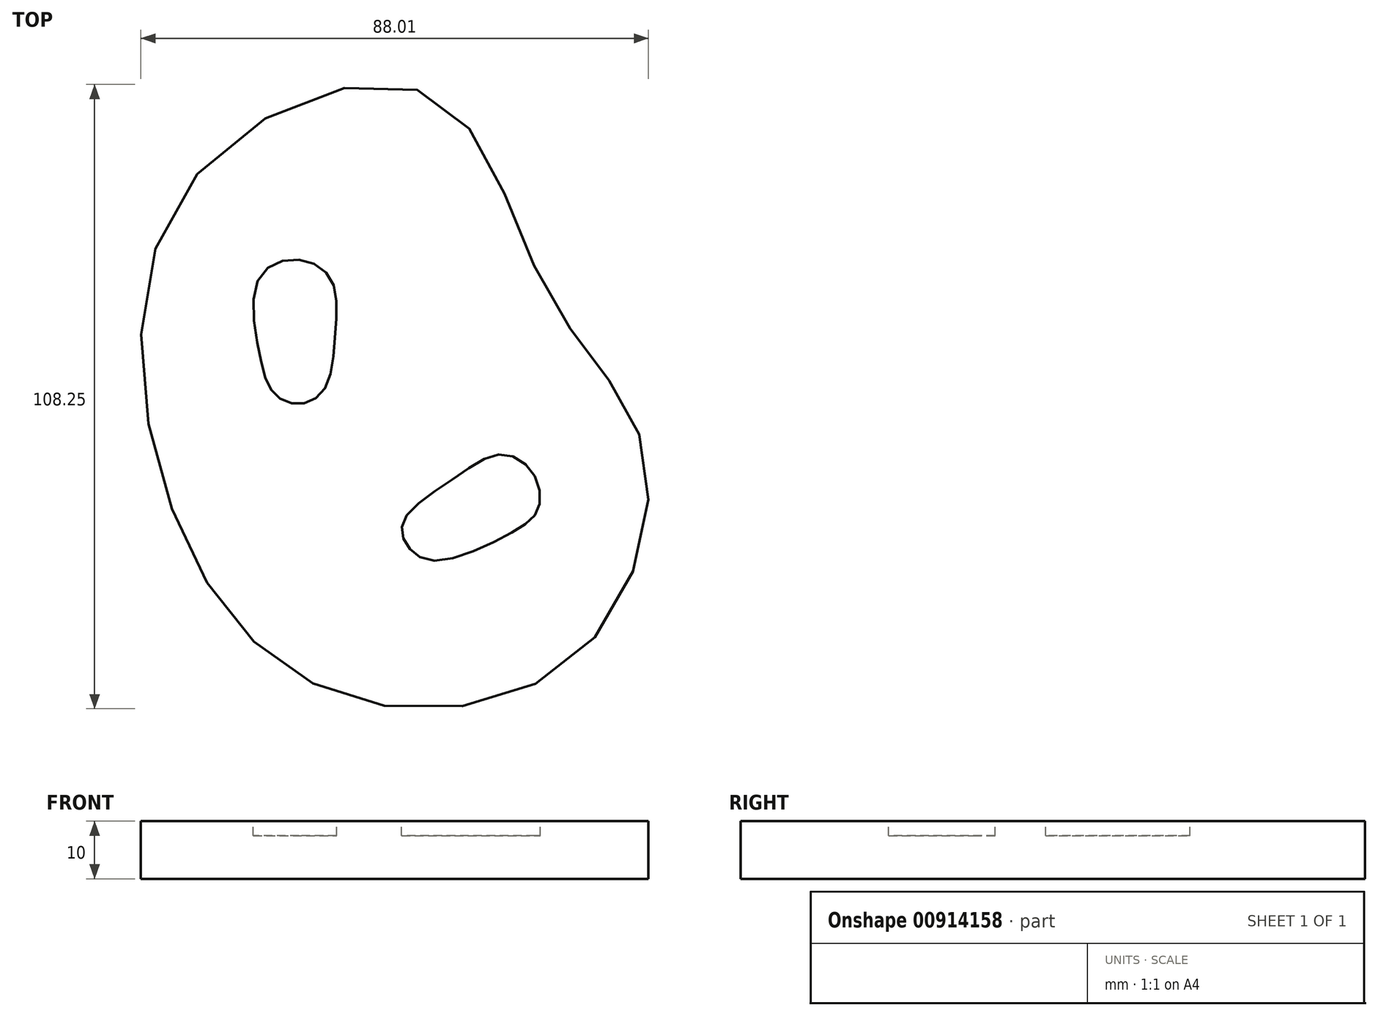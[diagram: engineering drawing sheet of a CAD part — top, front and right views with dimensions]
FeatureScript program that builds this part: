
annotation { "Feature Type Name" : "Feature", "Feature Type Description" : "" }
export const myFeature = defineFeature(function(context is Context, id is Id, definition is map)
    precondition{}
    {
        {
            assignVariable(context, id + "F0", {"name" : "h", "anyValue" : 10});
        }
        {
            var Q0;
            Q0=qCreatedBy(makeId("Top.planeOp"),FACE);
            var sketch = newSketch(context, id + "F1", { "sketchPlane" : qUnion([Q0])});
            skFitSpline(sketch, "E0", {"points": [v(-10.35, 25.21) * mm, v(-17.36, 21.86) * mm, v(-17.11, 8.64) * mm, v(-14.67, 2) * mm, v(-10.22, 0.21) * mm, v(-5.84, 2.85) * mm, v(-4.07, 12.17) * mm, v(-4.62, 21.5) * mm, v(-10.35, 25.21) * mm]});
            skFitSpline(sketch, "E1", {"points": [v(30.6, -12.37) * mm, v(25.06, -8.55) * mm, v(16.65, -12.63) * mm, v(7.87, -19.95) * mm, v(8.26, -24.1) * mm, v(13.05, -27.02) * mm, v(26.1, -22.38) * mm, v(31.03, -18.3) * mm, v(30.6, -12.37) * mm]});
            skFitSpline(sketch, "E2", {"points": [v(-32.35, -18.03) * mm, v(-30.03, 37.4) * mm, v(12.27, 53.8) * mm, v(32.75, 19.5) * mm, v(49.52, -8) * mm, v(37.14, -44.12) * mm, v(-4.42, -49.84) * mm, v(-32.35, -18.03) * mm]});
            skLineSegment(sketch, "E3", {"start": v(-10.35, 25.21) * mm, "end": v(-10.22, 0.21) * mm, "construction": true});
            skLineSegment(sketch, "E4", {"start": v(8.26, -24.1) * mm, "end": v(30.6, -12.37) * mm, "construction": true});
            skFitSpline(sketch, "E5.0", {"points": [v(-25.37, -18.06) * mm, v(-26.26, -15.78) * mm, v(-27.1, -13.42) * mm, v(-28.13, -10.2) * mm, v(-29.26, -6.07) * mm, v(-30.3, -1) * mm, v(-31.23, 5.83) * mm, v(-31.38, 12.6) * mm, v(-30.64, 19) * mm, v(-29.61, 23.58) * mm, v(-28.1, 27.85) * mm, v(-26.58, 30.8) * mm, v(-25.4, 32.68) * mm, v(-24.79, 33.59) * mm, v(-24.13, 34.48) * mm, v(-23.2, 35.65) * mm, v(-21.92, 37.08) * mm, v(-19.7, 39.27) * mm, v(-16.63, 41.8) * mm, v(-12.58, 44.39) * mm, v(-8.33, 46.48) * mm, v(-4.06, 48) * mm, v(0.06, 48.9) * mm, v(3.2, 49.14) * mm, v(5.43, 49.02) * mm, v(6.95, 48.79) * mm, v(8.07, 48.5) * mm, v(8.88, 48.2) * mm, v(9.44, 47.96) * mm, v(9.97, 47.7) * mm, v(10.66, 47.29) * mm, v(11.5, 46.67) * mm, v(12.52, 45.76) * mm, v(13.86, 44.28) * mm, v(15.51, 41.93) * mm, v(17.41, 38.43) * mm, v(19.24, 34.4) * mm, v(21.03, 30) * mm, v(22.56, 26.15) * mm, v(23.85, 23.05) * mm, v(24.88, 20.72) * mm, v(25.8, 18.8) * mm, v(26.56, 17.27) * mm, v(27.17, 16.13) * mm, v(27.8, 15.03) * mm, v(28.64, 13.6) * mm, v(29.73, 11.88) * mm, v(31.05, 9.94) * mm, v(32.8, 7.5) * mm, v(34.96, 4.66) * mm, v(37.35, 1.55) * mm, v(39.44, -1.36) * mm, v(40.86, -3.67) * mm, v(41.79, -5.48) * mm, v(42.38, -6.84) * mm, v(42.78, -7.98) * mm, v(43.05, -8.91) * mm, v(43.23, -9.62) * mm, v(43.38, -10.36) * mm, v(43.55, -11.39) * mm, v(43.7, -12.74) * mm, v(43.78, -14.45) * mm, v(43.73, -16.83) * mm, v(43.38, -19.95) * mm, v(42.5, -23.79) * mm, v(41.19, -27.58) * mm, v(39.45, -31.2) * mm, v(37.67, -34) * mm, v(36.08, -36.03) * mm, v(34.8, -37.45) * mm, v(33.67, -38.54) * mm, v(32.74, -39.34) * mm, v(31.28, -40.5) * mm, v(28.9, -42.05) * mm, v(25.36, -43.73) * mm, v(21.52, -44.98) * mm, v(16.1, -46.09) * mm, v(10.43, -46.32) * mm, v(4.9, -45.7) * mm, v(1.56, -44.97) * mm, v(-0.97, -44.19) * mm, v(-2.8, -43.52) * mm, v(-4.54, -42.75) * mm, v(-6.8, -41.6) * mm, v(-9.46, -39.95) * mm, v(-13.43, -36.8) * mm, v(-17.91, -31.95) * mm, v(-21.77, -25.86) * mm, v(-24.13, -21) * mm, v(-25.37, -18.06) * mm, v(-26.26, -15.78) * mm, v(-27.1, -13.42) * mm, v(-25.37, -18.06) * mm]});
            skFitSpline(sketch, "E6.0", {"points": [v(-21.2, -16.37) * mm, v(-22.04, -14.21) * mm, v(-22.83, -11.98) * mm, v(-23.8, -8.94) * mm, v(-24.88, -5.02) * mm, v(-25.86, -0.23) * mm, v(-26.52, 4.57) * mm, v(-26.8, 9.31) * mm, v(-26.7, 13.9) * mm, v(-26.2, 18.27) * mm, v(-25.27, 22.34) * mm, v(-24.17, 25.46) * mm, v(-23.08, 27.77) * mm, v(-22.31, 29.15) * mm, v(-21.65, 30.2) * mm, v(-21.12, 30.98) * mm, v(-20.56, 31.74) * mm, v(-19.75, 32.74) * mm, v(-18.66, 33.98) * mm, v(-16.72, 35.9) * mm, v(-13.98, 38.14) * mm, v(-10.36, 40.46) * mm, v(-6.57, 42.33) * mm, v(-2.8, 43.67) * mm, v(0.15, 44.32) * mm, v(2.28, 44.55) * mm, v(3.73, 44.6) * mm, v(5, 44.53) * mm, v(5.89, 44.4) * mm, v(6.49, 44.26) * mm, v(6.89, 44.14) * mm, v(7.24, 44.01) * mm, v(7.53, 43.89) * mm, v(7.8, 43.75) * mm, v(8.07, 43.59) * mm, v(8.36, 43.4) * mm, v(8.76, 43.09) * mm, v(9.31, 42.59) * mm, v(10.04, 41.78) * mm, v(10.83, 40.75) * mm, v(11.94, 39.08) * mm, v(13.36, 36.46) * mm, v(15.1, 32.64) * mm, v(16.55, 29.05) * mm, v(17.77, 26.01) * mm, v(18.72, 23.67) * mm, v(19.72, 21.28) * mm, v(20.6, 19.26) * mm, v(21.36, 17.64) * mm, v(21.95, 16.42) * mm, v(22.57, 15.2) * mm, v(23.23, 13.97) * mm, v(23.9, 12.78) * mm, v(24.8, 11.24) * mm, v(25.97, 9.41) * mm, v(27.36, 7.36) * mm, v(28.74, 5.44) * mm, v(30.08, 3.65) * mm, v(31.8, 1.4) * mm, v(33.76, -1.16) * mm, v(35.71, -3.89) * mm, v(36.95, -5.91) * mm, v(37.72, -7.41) * mm, v(38.19, -8.5) * mm, v(38.5, -9.37) * mm, v(38.7, -10.08) * mm, v(38.84, -10.62) * mm, v(38.96, -11.19) * mm, v(39.1, -12) * mm, v(39.21, -13.08) * mm, v(39.27, -14.5) * mm, v(39.23, -16.5) * mm, v(38.94, -19.2) * mm, v(38.17, -22.54) * mm, v(37.02, -25.86) * mm, v(35.5, -29.02) * mm, v(33.97, -31.42) * mm, v(32.62, -33.14) * mm, v(31.56, -34.33) * mm, v(30.63, -35.22) * mm, v(29.87, -35.87) * mm, v(29.08, -36.5) * mm, v(28.02, -37.25) * mm, v(26.2, -38.34) * mm, v(23.7, -39.53) * mm, v(20.37, -40.62) * mm, v(16.8, -41.35) * mm, v(13.08, -41.7) * mm, v(9.32, -41.66) * mm, v(6.24, -41.32) * mm, v(3.86, -40.86) * mm, v(2.13, -40.43) * mm, v(0.47, -39.92) * mm, v(-1.11, -39.34) * mm, v(-2.62, -38.68) * mm, v(-4.56, -37.7) * mm, v(-6.86, -36.26) * mm, v(-10.32, -33.53) * mm, v(-13.5, -30.09) * mm, v(-16.42, -25.89) * mm, v(-18.46, -22.37) * mm, v(-20.03, -19.13) * mm, v(-21.2, -16.37) * mm, v(-22.04, -14.21) * mm, v(-22.83, -11.98) * mm, v(-21.2, -16.37) * mm]});
            skFitSpline(sketch, "E7.0", {"points": [v(-18.42, -15.24) * mm, v(-19.23, -13.17) * mm, v(-19.99, -11.02) * mm, v(-20.93, -8.1) * mm, v(-21.96, -4.33) * mm, v(-22.9, 0.28) * mm, v(-23.53, 4.87) * mm, v(-23.8, 9.37) * mm, v(-23.7, 13.7) * mm, v(-23.23, 17.77) * mm, v(-22.38, 21.52) * mm, v(-21.38, 24.33) * mm, v(-20.4, 26.4) * mm, v(-19.73, 27.62) * mm, v(-19.14, 28.56) * mm, v(-18.67, 29.24) * mm, v(-18.18, 29.9) * mm, v(-17.46, 30.8) * mm, v(-16.48, 31.91) * mm, v(-14.72, 33.65) * mm, v(-12.22, 35.7) * mm, v(-8.88, 37.84) * mm, v(-5.39, 39.56) * mm, v(-1.95, 40.78) * mm, v(0.68, 41.36) * mm, v(2.5, 41.56) * mm, v(3.7, 41.6) * mm, v(4.7, 41.54) * mm, v(5.34, 41.44) * mm, v(5.73, 41.35) * mm, v(5.97, 41.28) * mm, v(6.11, 41.23) * mm, v(6.2, 41.2) * mm, v(6.28, 41.16) * mm, v(6.34, 41.12) * mm, v(6.46, 41.05) * mm, v(6.6, 40.96) * mm, v(6.82, 40.8) * mm, v(7.18, 40.47) * mm, v(7.72, 39.87) * mm, v(8.38, 39.02) * mm, v(9.34, 37.56) * mm, v(10.67, 35.14) * mm, v(12.33, 31.47) * mm, v(13.77, 27.93) * mm, v(14.99, 24.9) * mm, v(15.94, 22.53) * mm, v(16.96, 20.1) * mm, v(17.87, 18.03) * mm, v(18.65, 16.35) * mm, v(19.26, 15.09) * mm, v(19.91, 13.81) * mm, v(20.6, 12.53) * mm, v(21.3, 11.27) * mm, v(22.02, 10.07) * mm, v(22.74, 8.9) * mm, v(23.7, 7.4) * mm, v(24.9, 5.64) * mm, v(26.32, 3.67) * mm, v(27.69, 1.84) * mm, v(29.42, -0.43) * mm, v(31.36, -2.96) * mm, v(32.91, -5.14) * mm, v(33.9, -6.67) * mm, v(34.51, -7.73) * mm, v(35, -8.7) * mm, v(35.33, -9.45) * mm, v(35.55, -10.02) * mm, v(35.69, -10.44) * mm, v(35.8, -10.87) * mm, v(35.91, -11.28) * mm, v(36, -11.74) * mm, v(36.12, -12.4) * mm, v(36.22, -13.3) * mm, v(36.27, -14.52) * mm, v(36.24, -16.28) * mm, v(35.97, -18.68) * mm, v(35.28, -21.7) * mm, v(34.24, -24.72) * mm, v(32.87, -27.57) * mm, v(31.5, -29.7) * mm, v(30.32, -31.21) * mm, v(29.4, -32.24) * mm, v(28.6, -33) * mm, v(27.96, -33.56) * mm, v(27.29, -34.1) * mm, v(26.38, -34.73) * mm, v(24.8, -35.68) * mm, v(22.6, -36.73) * mm, v(19.6, -37.71) * mm, v(16.36, -38.38) * mm, v(12.96, -38.7) * mm, v(9.5, -38.66) * mm, v(6.67, -38.34) * mm, v(4.5, -37.93) * mm, v(2.93, -37.54) * mm, v(1.42, -37.08) * mm, v(0.01, -36.56) * mm, v(-1.34, -35.97) * mm, v(-3.07, -35.09) * mm, v(-5.12, -33.8) * mm, v(-8.24, -31.34) * mm, v(-11.16, -28.2) * mm, v(-13.88, -24.28) * mm, v(-15.8, -20.96) * mm, v(-17.3, -17.88) * mm, v(-18.42, -15.24) * mm, v(-19.23, -13.17) * mm, v(-19.99, -11.02) * mm, v(-18.42, -15.24) * mm]});
            skSolve(sketch);
        }
        {
            var Q0;
            Q0=makeQuery(id+"F1.imprint","IMPRINT",FACE,{"disambiguationData":[TD([[makeQuery(id+"F1.imprint","IMPRINT",EDGE,{"derivedFrom":sQuery(id+"F1.wireOp",EDGE,"E2")}),-1.0]])]});
            var Q1;
            Q1=makeQuery(id+"F1.imprint","IMPRINT",FACE,{"disambiguationData":[TD([[makeQuery(id+"F1.imprint","IMPRINT",EDGE,{"derivedFrom":sQuery(id+"F1.wireOp",EDGE,"E5.0")}),-1.0]])]});
            var Q2;
            Q2=makeQuery(id+"F1.imprint","IMPRINT",FACE,{"disambiguationData":[TD([[makeQuery(id+"F1.imprint","IMPRINT",EDGE,{"derivedFrom":sQuery(id+"F1.wireOp",EDGE,"E6.0")}),-1.0]])]});
            var Q3;
            Q3=makeQuery(id+"F1.imprint","IMPRINT",FACE,{"disambiguationData":[TD([[makeQuery(id+"F1.imprint","IMPRINT",EDGE,{"derivedFrom":sQuery(id+"F1.wireOp",EDGE,"E0")}),-1.0]])]});
            var Q4;
            Q4=makeQuery(id+"F1.imprint","IMPRINT",FACE,{"disambiguationData":[TD([[makeQuery(id+"F1.imprint","IMPRINT",EDGE,{"derivedFrom":sQuery(id+"F1.wireOp",EDGE,"E0")}),1.0]])]});
            var Q5;
            Q5=makeQuery(id+"F1.imprint","IMPRINT",FACE,{"disambiguationData":[TD([[makeQuery(id+"F1.imprint","IMPRINT",EDGE,{"derivedFrom":sQuery(id+"F1.wireOp",EDGE,"E1")}),1.0]])]});
            extrude(context, id + "F2", {"entities" : qUnion([Q0, Q1, Q2, Q3, Q4, Q5]), "depth" : (getVariable(context, 'h') * 0.25) * mm, "offsetDistance" : 25 * mm});
        }
        {
            var Q0;
            Q0=makeQuery(id+"F1.imprint","IMPRINT",FACE,{"disambiguationData":[TD([[makeQuery(id+"F1.imprint","IMPRINT",EDGE,{"derivedFrom":sQuery(id+"F1.wireOp",EDGE,"E5.0")}),-1.0]])]});
            var Q1;
            Q1=makeQuery(id+"F1.imprint","IMPRINT",FACE,{"disambiguationData":[TD([[makeQuery(id+"F1.imprint","IMPRINT",EDGE,{"derivedFrom":sQuery(id+"F1.wireOp",EDGE,"E6.0")}),-1.0]])]});
            var Q2;
            Q2=makeQuery(id+"F1.imprint","IMPRINT",FACE,{"disambiguationData":[TD([[makeQuery(id+"F1.imprint","IMPRINT",EDGE,{"derivedFrom":sQuery(id+"F1.wireOp",EDGE,"E0")}),-1.0]])]});
            var Q3;
            Q3=makeQuery(id+"F1.imprint","IMPRINT",FACE,{"disambiguationData":[TD([[makeQuery(id+"F1.imprint","IMPRINT",EDGE,{"derivedFrom":sQuery(id+"F1.wireOp",EDGE,"E0")}),1.0]])]});
            var Q4;
            Q4=makeQuery(id+"F1.imprint","IMPRINT",FACE,{"disambiguationData":[TD([[makeQuery(id+"F1.imprint","IMPRINT",EDGE,{"derivedFrom":sQuery(id+"F1.wireOp",EDGE,"E1")}),1.0]])]});
            extrude(context, id + "F3", {"entities" : qUnion([Q0, Q1, Q2, Q3, Q4]), "operationType" : NewBodyOperationType.ADD, "depth" : (getVariable(context, 'h') * 0.5) * mm, "offsetDistance" : 25 * mm});
        }
        {
            var Q0;
            Q0=makeQuery(id+"F1.imprint","IMPRINT",FACE,{"disambiguationData":[TD([[makeQuery(id+"F1.imprint","IMPRINT",EDGE,{"derivedFrom":sQuery(id+"F1.wireOp",EDGE,"E6.0")}),-1.0]])]});
            var Q1;
            Q1=makeQuery(id+"F1.imprint","IMPRINT",FACE,{"disambiguationData":[TD([[makeQuery(id+"F1.imprint","IMPRINT",EDGE,{"derivedFrom":sQuery(id+"F1.wireOp",EDGE,"E0")}),-1.0]])]});
            var Q2;
            Q2=makeQuery(id+"F1.imprint","IMPRINT",FACE,{"disambiguationData":[TD([[makeQuery(id+"F1.imprint","IMPRINT",EDGE,{"derivedFrom":sQuery(id+"F1.wireOp",EDGE,"E0")}),1.0]])]});
            var Q3;
            Q3=makeQuery(id+"F1.imprint","IMPRINT",FACE,{"disambiguationData":[TD([[makeQuery(id+"F1.imprint","IMPRINT",EDGE,{"derivedFrom":sQuery(id+"F1.wireOp",EDGE,"E1")}),1.0]])]});
            extrude(context, id + "F4", {"entities" : qUnion([Q0, Q1, Q2, Q3]), "operationType" : NewBodyOperationType.ADD, "depth" : (getVariable(context, 'h') * 0.75) * mm, "offsetDistance" : 25 * mm});
        }
        {
            var Q0;
            Q0=makeQuery(id+"F1.imprint","IMPRINT",FACE,{"disambiguationData":[TD([[makeQuery(id+"F1.imprint","IMPRINT",EDGE,{"derivedFrom":sQuery(id+"F1.wireOp",EDGE,"E0")}),-1.0]])]});
            extrude(context, id + "F5", {"entities" : qUnion([Q0]), "operationType" : NewBodyOperationType.ADD, "depth" : (getVariable(context, 'h')) * mm, "offsetDistance" : 25 * mm});
        }
    });
